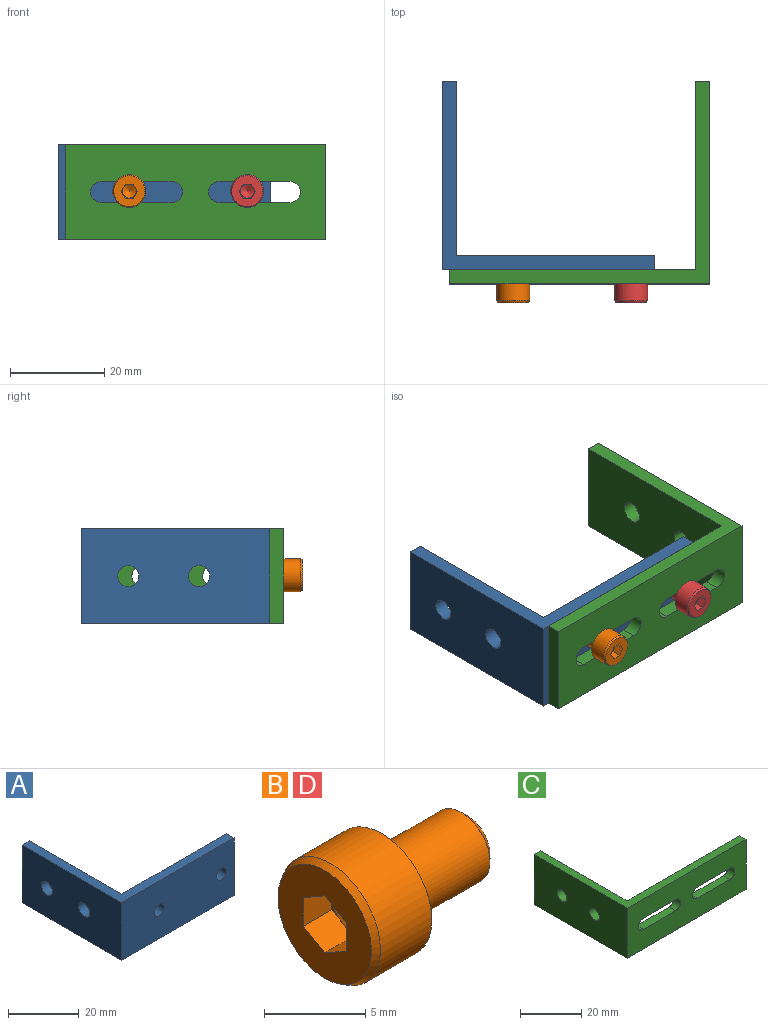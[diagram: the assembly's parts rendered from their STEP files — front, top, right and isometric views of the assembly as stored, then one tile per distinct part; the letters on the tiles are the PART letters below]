
ASSEMBLY  parts=4 mates=3
PART A: 12 faces, bbox 45x40x20 mm
  f0: plane 42x20mm, normal (0,1,0), area 814.9mm2, adj f3,f4,f6,f9,f10,f11
  f1: plane 45x20mm, normal (0,-1,0), area 874.9mm2, adj f2,f3,f4,f9,f10,f11
  f2: plane 40x20mm, normal (-1,0,0), area 768.2mm2, adj f1,f3,f4,f5,f7,f8
  f3: plane 45x40mm, normal (0,0,-1), area 246mm2, adj f0,f1,f2,f5,f6,f11
  f4: plane 45x40mm, normal (0,0,1), area 246mm2, adj f0,f1,f2,f5,f6,f11
  f5: plane 20x3mm, normal (0,1,0), area 60mm2, adj f2,f3,f4,f6
  f6: plane 37x20mm, normal (1,0,0), area 708.2mm2, adj f0,f3,f4,f5,f7,f8
  f7: cylinder r=2.25mm len=4.5mm, axis (-1,0,0), area 42.4mm2, adj f2,f6
  f8: cylinder r=2.25mm len=4.5mm, axis (-1,0,0), area 42.4mm2, adj f2,f6
  f9: cylinder r=2mm len=4mm, axis (0,-1,0), area 37.7mm2, adj f0,f1
  f10: cylinder r=2mm len=4mm, axis (0,-1,0), area 37.7mm2, adj f0,f1
  f11: plane 20x3mm, normal (1,0,0), area 60mm2, adj f0,f1,f3,f4
PART B: 21 faces, bbox 10x7x7 mm
  f0: cone r=3.27mm half-angle=30deg, axis (1,0,0), area 9.8mm2, adj f1,f14
  f1: plane 6.54x6.54mm, normal (-1,0,0), area 25.8mm2, adj f0,f2,f3,f4,f5,f6,f7
  f2: plane 2x1.5mm, normal (0,-0.5,-0.87), area 3.5mm2, adj f1,f3,f4,f17,f18
  f3: plane 2x1.5mm, normal (0,0.5,-0.87), area 3.5mm2, adj f1,f2,f7,f18,f19
  f4: plane 2x1.73mm, normal (0,-1,0), area 3.5mm2, adj f1,f2,f5,f15,f17
  f5: plane 2x1.5mm, normal (0,-0.5,0.87), area 3.5mm2, adj f1,f4,f6,f15,f16
  f6: plane 2x1.5mm, normal (0,0.5,0.87), area 3.5mm2, adj f1,f5,f7,f16,f20
  f7: plane 2x1.73mm, normal (0,1,0), area 3.5mm2, adj f1,f3,f6,f19,f20
  f8: cone r=1.5mm half-angle=60deg, axis (-1,0,0), area 8.2mm2, adj f15,f16,f17,f18,f19,f20
  f9: plane 3.14x3.14mm, normal (1,0,0), area 7.7mm2, adj f10
  f10: cone r=2mm half-angle=45deg, axis (-1,0,0), area 6.8mm2, adj f9,f11
  f11: cylinder r=2mm len=5.37mm, axis (-1,0,0), area 67.5mm2, adj f10,f12
  f12: torus R=2.2mm, axis (1,0,0), area 4.1mm2, adj f11,f13
  f13: plane 7x7mm, normal (1,0,0), area 23.3mm2, adj f12,f14
  f14: cylinder r=3.5mm len=7mm, axis (-1,0,0), area 79.2mm2, adj f0,f13
  f15: plane 1.3x0.75mm, normal (-1,0,0), area 0.1mm2, adj f4,f5,f8
  f16: plane 1.5x0.43mm, normal (-1,0,0), area 0.1mm2, adj f5,f6,f8
  f17: plane 1.3x0.75mm, normal (-1,0,0), area 0.1mm2, adj f2,f4,f8
  f18: plane 1.5x0.43mm, normal (-1,0,0), area 0.1mm2, adj f2,f3,f8
  f19: plane 1.3x0.75mm, normal (-1,0,0), area 0.1mm2, adj f3,f7,f8
  f20: plane 1.3x0.75mm, normal (-1,0,0), area 0.1mm2, adj f6,f7,f8
PART C: 18 faces, bbox 55x43x20 mm
  f0: plane 52x20mm, normal (0,1,0), area 873.2mm2, adj f3,f4,f5,f6,f9,f10,f11,f12
  f1: plane 55x20mm, normal (0,-1,0), area 933.2mm2, adj f2,f3,f4,f5,f9,f10,f11,f12
  f2: plane 43x20mm, normal (-1,0,0), area 828.2mm2, adj f1,f3,f5,f7,f8,f17
  f3: plane 55x43mm, normal (0,0,-1), area 285mm2, adj f0,f1,f2,f4,f6,f17
  f4: plane 20x3mm, normal (1,0,0), area 60mm2, adj f0,f1,f3,f5
  f5: plane 55x43mm, normal (0,0,1), area 285mm2, adj f0,f1,f2,f4,f6,f17
  f6: plane 40x20mm, normal (1,0,0), area 768.2mm2, adj f0,f3,f5,f7,f8,f17
  f7: cylinder r=2.25mm len=4.5mm, axis (-1,0,0), area 42.4mm2, adj f2,f6
  f8: cylinder r=2.25mm len=4.5mm, axis (-1,0,0), area 42.4mm2, adj f2,f6
  f9: plane 15x3mm, normal (0,0,-1), area 45mm2, adj f0,f1,f10,f12
  f10: cylinder r=2.25mm len=4.5mm, axis (0,-1,0), area 21.2mm2, adj f0,f1,f9,f11
  f11: plane 15x3mm, normal (0,0,1), area 45mm2, adj f0,f1,f10,f12
  f12: cylinder r=2.25mm len=4.5mm, axis (0,-1,0), area 21.2mm2, adj f0,f1,f9,f11
  f13: plane 15x3mm, normal (0,0,1), area 45mm2, adj f0,f1,f14,f16
  f14: cylinder r=2.25mm len=4.5mm, axis (0,-1,0), area 21.2mm2, adj f0,f1,f13,f15
  f15: plane 15x3mm, normal (0,0,-1), area 45mm2, adj f0,f1,f14,f16
  f16: cylinder r=2.25mm len=4.5mm, axis (0,-1,0), area 21.2mm2, adj f0,f1,f13,f15
  f17: plane 20x3mm, normal (0,1,0), area 60mm2, adj f2,f3,f5,f6
PART D: same geometry as B
PLACE A t=(10.59,-7.39,9.57)mm fixed
PLACE B rot(axis=(0.58,0.58,0.58),120deg) t=(-1.94,-13.39,9.77)mm
PLACE C rot(axis=(0,1,0),180deg) t=(12.12,-10.39,9.57)mm
PLACE D rot(axis=(0.58,0.58,0.58),120deg) t=(23.06,-13.39,9.77)mm
MATE parallel B.f0 <-> C.f1  axis (0,1,0) through (-1.94,-13.39,9.77)mm
MATE parallel C.f0 <-> A.f1  axis (0,1,0) through (10.34,-10.39,9.57)mm
MATE parallel C.f5 <-> A.f3  axis (0,0,-1) through (23.07,-2.84,-0.43)mm
